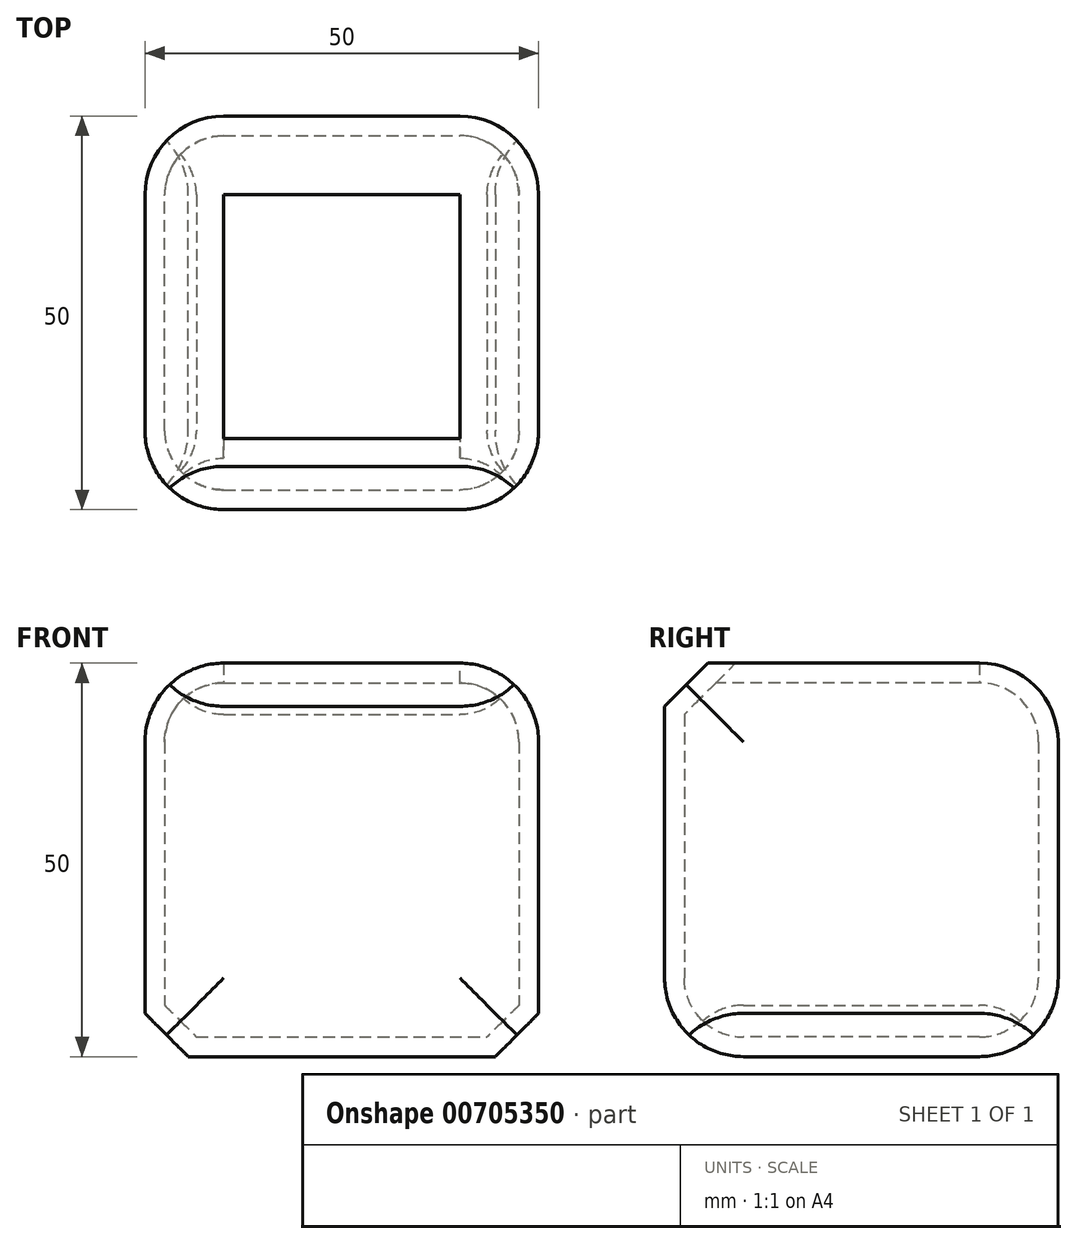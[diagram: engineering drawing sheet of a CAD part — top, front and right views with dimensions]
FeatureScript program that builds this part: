
annotation { "Feature Type Name" : "Feature", "Feature Type Description" : "" }
export const myFeature = defineFeature(function(context is Context, id is Id, definition is map)
    precondition{}
    {
        {
            var Q0;
            Q0=qCreatedBy(makeId("Top.planeOp"),FACE);
            var sketch = newSketch(context, id + "F0", { "sketchPlane" : qUnion([Q0])});
            skLineSegment(sketch, "E0.bottom", {"start": v(25, 25) * mm, "end": v(-25, 25) * mm});
            skLineSegment(sketch, "E0.top", {"start": v(25, -25) * mm, "end": v(-25, -25) * mm});
            skLineSegment(sketch, "E0.left", {"start": v(25, 25) * mm, "end": v(25, -25) * mm});
            skLineSegment(sketch, "E0.right", {"start": v(-25, 25) * mm, "end": v(-25, -25) * mm});
            skPoint(sketch, "E0.middle", {"position": v(0, 0) * mm});
            skSolve(sketch);
        }
        {
            var Q0;
            Q0 = qSketchRegion(id + "F0", true);
            extrude(context, id + "F1", {"entities" : qUnion([Q0]), "depth" : 50 * mm, "offsetDistance" : 25 * mm});
        }
        {
            var Q0;
            Q0=makeQuery(id+"F1.opExtrude","SWEPT_EDGE",EDGE,{"disambiguationData":[OSD([sQuery(id+"F0.wireOp",EDGE,"E0.top"),sQuery(id+"F0.wireOp",EDGE,"E0.left")])]});
            var Q1;
            Q1=makeQuery(id+"F1.opExtrude","SWEPT_EDGE",EDGE,{"disambiguationData":[OSD([sQuery(id+"F0.wireOp",EDGE,"E0.top"),sQuery(id+"F0.wireOp",EDGE,"E0.right")])]});
            var Q2;
            Q2=makeQuery(id+"F1.opExtrude","SWEPT_EDGE",EDGE,{"disambiguationData":[OSD([sQuery(id+"F0.wireOp",EDGE,"E0.bottom"),sQuery(id+"F0.wireOp",EDGE,"E0.right")])]});
            var Q3;
            Q3=makeQuery(id+"F1.opExtrude","SWEPT_EDGE",EDGE,{"disambiguationData":[OSD([sQuery(id+"F0.wireOp",EDGE,"E0.bottom"),sQuery(id+"F0.wireOp",EDGE,"E0.left")])]});
            var Q4;
            Q4=makeQuery(id+"F1.opExtrude","CAP_EDGE",EDGE,{"disambiguationData":[OSD([sQuery(id+"F0.wireOp",EDGE,"E0.left")])],"isStart":false});
            var Q5;
            Q5=makeQuery(id+"F1.opExtrude","CAP_EDGE",EDGE,{"disambiguationData":[OSD([sQuery(id+"F0.wireOp",EDGE,"E0.right")])],"isStart":false});
            var Q6;
            Q6=makeQuery(id+"F1.opExtrude","CAP_EDGE",EDGE,{"disambiguationData":[OSD([sQuery(id+"F0.wireOp",EDGE,"E0.top")])],"isStart":true});
            var Q7;
            Q7=makeQuery(id+"F1.opExtrude","SWEPT_FACE",FACE,{"disambiguationData":[OSD([sQuery(id+"F0.wireOp",EDGE,"E0.bottom")])]});
            var Q8;
            Q8=makeQuery(id+"F1.opExtrude","CAP_EDGE",EDGE,{"disambiguationData":[OSD([sQuery(id+"F0.wireOp",EDGE,"E0.bottom")])],"isStart":true});
            fillet(context, id + "F2", {"entities" : qUnion([Q0, Q1, Q2, Q3, Q4, Q5, Q6, Q7, Q8]), "radius" : 10 * mm, "tangentPropagation" : true, "allowEdgeOverflow" : false});
        }
        {
            var Q0;
            Q0=makeQuery(id+"F1.opExtrude","CAP_FACE",FACE,{"disambiguationData":[OSD([sQuery(id+"F0.wireOp",EDGE,"E0.bottom"),sQuery(id+"F0.wireOp",EDGE,"E0.top"),sQuery(id+"F0.wireOp",EDGE,"E0.left"),sQuery(id+"F0.wireOp",EDGE,"E0.right")])],"isStart":false});
            var Q1;
            Q1=makeQuery(id+"F1.opExtrude","CAP_FACE",FACE,{"disambiguationData":[OSD([sQuery(id+"F0.wireOp",EDGE,"E0.bottom"),sQuery(id+"F0.wireOp",EDGE,"E0.top"),sQuery(id+"F0.wireOp",EDGE,"E0.left"),sQuery(id+"F0.wireOp",EDGE,"E0.right")])],"isStart":true});
            var Q2;
            {var subQ0=sQuery(id+"F0.wireOp",EDGE,"E0.bottom");Q2=makeQuery(id+"F2.opFillet","BLEND_FACE",FACE,{"disambiguationData":[OSD([subQ0]),TDD([makeQuery(id+"F1.opExtrude","CAP_EDGE",EDGE,{"disambiguationData":[OSD([subQ0])],"isStart":false})])]});}
            chamfer(context, id + "F3", {"entities" : qUnion([Q0, Q1, Q2]), "width" : 5.5 * mm, "tangentPropagation" : true});
        }
        {
            var Q0;
            Q0=makeQuery(id+"F1.opExtrude","CAP_FACE",FACE,{"disambiguationData":[OSD([sQuery(id+"F0.wireOp",EDGE,"E0.bottom"),sQuery(id+"F0.wireOp",EDGE,"E0.top"),sQuery(id+"F0.wireOp",EDGE,"E0.left"),sQuery(id+"F0.wireOp",EDGE,"E0.right")])],"isStart":false});
            shell(context, id + "F4", {"entities" : qUnion([Q0]), "thickness" : 2.5 * mm});
        }
    });
